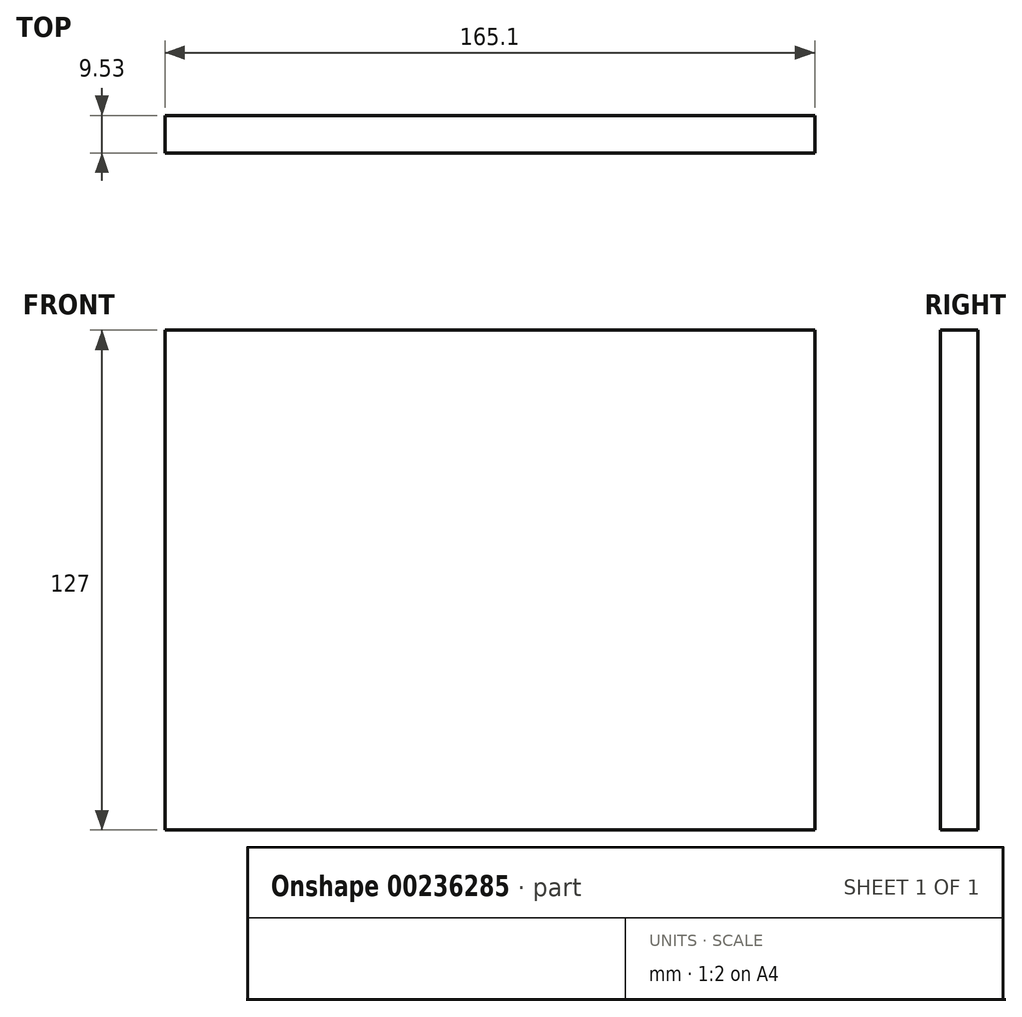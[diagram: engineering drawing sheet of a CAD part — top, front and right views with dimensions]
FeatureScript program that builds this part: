
annotation { "Feature Type Name" : "Feature", "Feature Type Description" : "" }
export const myFeature = defineFeature(function(context is Context, id is Id, definition is map)
    precondition{}
    {
        {
            var Q0;
            Q0=qCreatedBy(makeId("Front.planeOp"),FACE);
            var sketch = newSketch(context, id + "F0", { "sketchPlane" : qUnion([Q0])});
            skLineSegment(sketch, "E0.bottom", {"start": v(82.55, -63.5) * mm, "end": v(-82.55, -63.5) * mm});
            skLineSegment(sketch, "E0.top", {"start": v(82.55, 63.5) * mm, "end": v(-82.55, 63.5) * mm});
            skLineSegment(sketch, "E0.left", {"start": v(82.55, -63.5) * mm, "end": v(82.55, 63.5) * mm});
            skLineSegment(sketch, "E0.right", {"start": v(-82.55, -63.5) * mm, "end": v(-82.55, 63.5) * mm});
            skPoint(sketch, "E0.middle", {"position": v(0, 0) * mm});
            skSolve(sketch);
        }
        {
            var Q0;
            Q0=makeQuery(id+"F0.imprint","IMPRINT",FACE,{"disambiguationData":[TD([[makeQuery(id+"F0.imprint","IMPRINT",EDGE,{"derivedFrom":sQuery(id+"F0.wireOp",EDGE,"E0.bottom")}),-1.0]])]});
            extrude(context, id + "F1", {"entities" : qUnion([Q0]), "depth" : 9.52 * mm});
        }
    });
